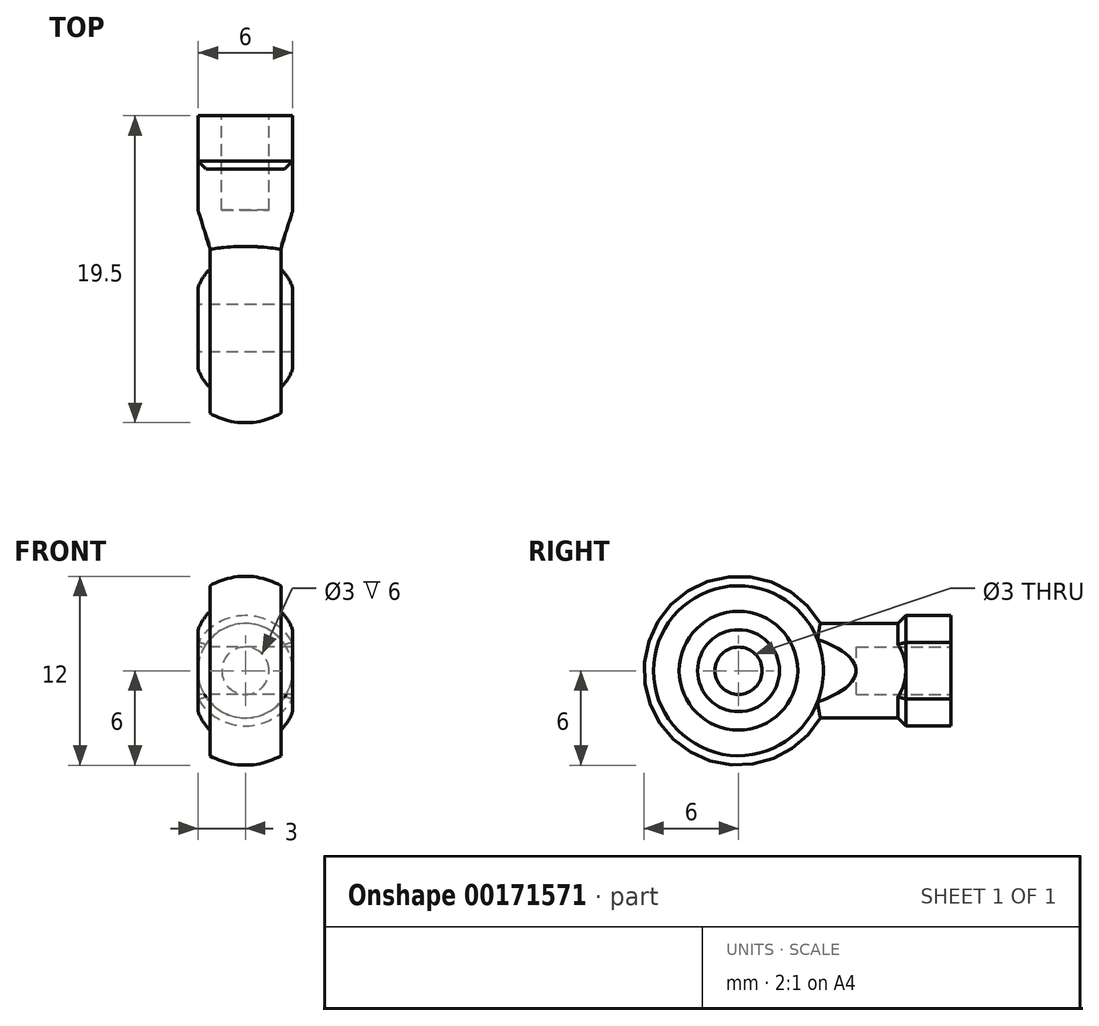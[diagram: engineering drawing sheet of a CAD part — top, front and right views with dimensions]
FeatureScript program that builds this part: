
annotation { "Feature Type Name" : "Feature", "Feature Type Description" : "" }
export const myFeature = defineFeature(function(context is Context, id is Id, definition is map)
    precondition{}
    {
        {
            assignVariable(context, id + "F0", {"name" : "L1", "anyValue" : 13.5});
        }
        {
            assignVariable(context, id + "F1", {"name" : "L2", "anyValue" : 6});
        }
        {
            assignVariable(context, id + "F2", {"name" : "AF", "anyValue" : 6});
        }
        {
            assignVariable(context, id + "F3", {"name" : "Wrench_Diam", "anyValue" : getVariable(context, 'AF') + 1});
        }
        {
            assignVariable(context, id + "F4", {"name" : "Chamfer_Size", "anyValue" : (getVariable(context, 'Wrench_Diam') - getVariable(context, 'AF')) / 2});
        }
        {
            var Q0;
            Q0=qCreatedBy(makeId("Top.planeOp"),FACE);
            var sketch = newSketch(context, id + "F5", { "sketchPlane" : qUnion([Q0])});
            skLineSegment(sketch, "E0", {"start": v(-3, 0) * mm, "end": v(3, 0) * mm, "construction": true});
            skLineSegment(sketch, "E1", {"start": v(-3, 1.5) * mm, "end": v(-3, 2.6) * mm});
            skArc(sketch, "E2", {"start": v(3, 2.6) * mm, "mid": v(0, 4.7) * mm, "end": v(-3, 2.6) * mm});
            skLineSegment(sketch, "E3", {"start": v(-3, 1.5) * mm, "end": v(3, 1.5) * mm});
            skLineSegment(sketch, "E4", {"start": v(3, 1.5) * mm, "end": v(3, 2.6) * mm});
            skLineSegment(sketch, "E5", {"start": v(-2.25, 3.77) * mm, "end": v(-2.25, 5.4) * mm});
            skArc(sketch, "E6", {"start": v(2.25, 5.4) * mm, "mid": v(0, 6) * mm, "end": v(-2.25, 5.4) * mm});
            skLineSegment(sketch, "E7", {"start": v(2.25, 5.4) * mm, "end": v(2.25, 3.77) * mm});
            skPoint(sketch, "E8.endSnap0", {"position": v(0, 4.7) * mm});
            skLineSegment(sketch, "E9", {"start": v(0, 0) * mm, "end": v(0, 6) * mm, "construction": true});
            skLineSegment(sketch, "E10", {"start": v(2.25, 5.4) * mm, "end": v(3.29, 8.25) * mm});
            skLineSegment(sketch, "E11", {"start": v(3.29, 8.25) * mm, "end": v(5, 8.25) * mm});
            skLineSegment(sketch, "E12", {"start": v(5, 8.25) * mm, "end": v(5, 1.5) * mm});
            skLineSegment(sketch, "E13", {"start": v(5, 1.5) * mm, "end": v(3, 1.5) * mm});
            skLineSegment(sketch, "E14.MirrorCS", {"start": v(-2.25, 5.4) * mm, "end": v(-3.29, 8.25) * mm});
            skLineSegment(sketch, "E15.MirrorCS", {"start": v(-3.29, 8.25) * mm, "end": v(-5, 8.25) * mm});
            skLineSegment(sketch, "E16.MirrorCS", {"start": v(-5, 8.25) * mm, "end": v(-5, 1.5) * mm});
            skLineSegment(sketch, "E17.MirrorCS", {"start": v(-5, 1.5) * mm, "end": v(-3, 1.5) * mm});
            skSolve(sketch);
        }
        {
            var Q0;
            {var subQ1=sQuery(id+"F5.wireOp",EDGE,"E1");Q0=makeQuery(id+"F5.imprint","IMPRINT",FACE,{"disambiguationData":[TD([[makeQuery(id+"F5.imprint","IMPRINT",EDGE,{"derivedFrom":subQ1}),-1.0]])]});}
            var Q1;
            {var subQ0=sQuery(id+"F5.wireOp",EDGE,"E5");Q1=makeQuery(id+"F5.imprint","IMPRINT",FACE,{"disambiguationData":[TD([[makeQuery(id+"F5.imprint","IMPRINT",EDGE,{"derivedFrom":subQ0}),-1.0]])]});}
            var Q2;
            Q2=sQuery(id+"F5.wireOp",EDGE,"E0");
            revolve(context, id + "F6", {"entities" : qUnion([Q0, Q1]), "axis" : qUnion([Q2]), "revolveType" : RevolveType.FULL});
        }
        {
            var Q0;
            Q0=qCreatedBy(makeId("Front.planeOp"),FACE);
            cPlane(context, id + "F7", {"entities" : qUnion([Q0]), "cplaneType" : CPlaneType.OFFSET, "offset" : (getVariable(context, 'L1')) * mm, "oppositeDirection" : true, "width" : 150 * mm, "height" : 150 * mm});
        }
        {
            var Q0;
            Q0=qCreatedBy(id+"F7.planeOp",FACE);
            var sketch = newSketch(context, id + "F8", { "sketchPlane" : qUnion([Q0])});
            skCircle(sketch, "E18", {"center": v(0, 0) * mm, "radius": 3 * mm});
            skArc(sketch, "E19", {"start": v(3, 1.8) * mm, "mid": v(0, 3.5) * mm, "end": v(-3, 1.8) * mm});
            skCircle(sketch, "E20", {"center": v(0, 0) * mm, "radius": 1.5 * mm});
            skLineSegment(sketch, "E21", {"start": v(3, -1.8) * mm, "end": v(3, 1.8) * mm});
            skLineSegment(sketch, "E22", {"start": v(-3, -1.8) * mm, "end": v(-3, 1.8) * mm});
            skArc(sketch, "E23.trimOffspring", {"start": v(-3, -1.8) * mm, "mid": v(0, -3.5) * mm, "end": v(3, -1.8) * mm});
            skArc(sketch, "E24", {"start": v(-3, 1.8) * mm, "mid": v(-3.5, 0) * mm, "end": v(-3, -1.8) * mm, "construction": true});
            skSolve(sketch);
        }
        {
            var Q0;
            Q0=makeQuery(id+"F8.imprint","IMPRINT",FACE,{"disambiguationData":[TD([[makeQuery(id+"F8.imprint","IMPRINT",EDGE,{"derivedFrom":sQuery(id+"F8.wireOp",EDGE,"E20")}),-1.0]])]});
            var Q1;
            Q1=makeQuery(id+"F8.imprint","IMPRINT",FACE,{"disambiguationData":[TD([[makeQuery(id+"F8.imprint","IMPRINT",EDGE,{"derivedFrom":sQuery(id+"F8.wireOp",EDGE,"E20")}),1.0]])]});
            extrude(context, id + "F9", {"entities" : qUnion([Q0, Q1]), "operationType" : NewBodyOperationType.ADD, "endBound" : BoundingType.UP_TO_NEXT, "depth" : 25 * mm});
        }
        {
            var Q0;
            {var subQ5=sQuery(id+"F8.wireOp",EDGE,"E19");Q0=makeQuery(id+"F8.imprint","IMPRINT",FACE,{"disambiguationData":[TD([[makeQuery(id+"F8.imprint","IMPRINT",EDGE,{"derivedFrom":subQ5}),1.0]])]});}
            var Q1;
            {var subQ5=sQuery(id+"F8.wireOp",EDGE,"E23.trimOffspring");Q1=makeQuery(id+"F8.imprint","IMPRINT",FACE,{"disambiguationData":[TD([[makeQuery(id+"F8.imprint","IMPRINT",EDGE,{"derivedFrom":subQ5}),1.0]])]});}
            extrude(context, id + "F10", {"entities" : qUnion([Q0, Q1]), "operationType" : NewBodyOperationType.ADD, "depth" : (getVariable(context, 'L1') / 4) * mm});
        }
        {
            var Q0;
            Q0=makeQuery(id+"F8.imprint","IMPRINT",FACE,{"disambiguationData":[TD([[makeQuery(id+"F8.imprint","IMPRINT",EDGE,{"derivedFrom":sQuery(id+"F8.wireOp",EDGE,"E20")}),1.0]])]});
            extrude(context, id + "F11", {"entities" : qUnion([Q0]), "operationType" : NewBodyOperationType.REMOVE, "depth" : (getVariable(context, 'L2')) * mm});
        }
        {
            var Q0;
            Q0=makeQuery(id+"F10.opExtrude","CAP_EDGE",EDGE,{"disambiguationData":[OSD([sQuery(id+"F8.wireOp",EDGE,"E19")])],"isStart":false});
            var Q1;
            {var subQ0=sQuery(id+"F8.wireOp",EDGE,"E21");Q1=makeQuery(id+"F10.opExtrude","CAP_EDGE",EDGE,{"disambiguationData":[OSD([subQ0]),TDD([makeQuery(id+"F8.imprint","IMPRINT",EDGE,{"disambiguationData":[TD([[makeQuery(id+"F8.imprint","INTERSECT",VERTEX,{"derivedFrom":[sQuery(id+"F8.wireOp",EDGE,"E19"),subQ0]}),1.0]])],"derivedFrom":subQ0})])],"isStart":false});}
            var Q2;
            {var subQ0=sQuery(id+"F8.wireOp",EDGE,"E22");Q2=makeQuery(id+"F10.opExtrude","CAP_EDGE",EDGE,{"disambiguationData":[OSD([subQ0]),TDD([makeQuery(id+"F8.imprint","IMPRINT",EDGE,{"disambiguationData":[TD([[makeQuery(id+"F8.imprint","INTERSECT",VERTEX,{"derivedFrom":[sQuery(id+"F8.wireOp",EDGE,"E19"),subQ0]}),1.0]])],"derivedFrom":subQ0})])],"isStart":false});}
            var Q3;
            Q3=makeQuery(id+"F10.opExtrude","CAP_EDGE",EDGE,{"disambiguationData":[OSD([sQuery(id+"F8.wireOp",EDGE,"E23.trimOffspring")])],"isStart":false});
            var Q4;
            {var subQ0=sQuery(id+"F8.wireOp",EDGE,"E21");Q4=makeQuery(id+"F10.opExtrude","CAP_EDGE",EDGE,{"disambiguationData":[OSD([subQ0]),TDD([makeQuery(id+"F8.imprint","IMPRINT",EDGE,{"disambiguationData":[TD([[makeQuery(id+"F8.imprint","INTERSECT",VERTEX,{"derivedFrom":[subQ0,sQuery(id+"F8.wireOp",EDGE,"E23.trimOffspring")]}),-1.0]])],"derivedFrom":subQ0})])],"isStart":false});}
            var Q5;
            {var subQ0=sQuery(id+"F8.wireOp",EDGE,"E22");Q5=makeQuery(id+"F10.opExtrude","CAP_EDGE",EDGE,{"disambiguationData":[OSD([subQ0]),TDD([makeQuery(id+"F8.imprint","IMPRINT",EDGE,{"disambiguationData":[TD([[makeQuery(id+"F8.imprint","INTERSECT",VERTEX,{"derivedFrom":[subQ0,sQuery(id+"F8.wireOp",EDGE,"E23.trimOffspring")]}),-1.0]])],"derivedFrom":subQ0})])],"isStart":false});}
            chamfer(context, id + "F12", {"entities" : qUnion([Q0, Q1, Q2, Q3, Q4, Q5]), "width" : (getVariable(context, 'Chamfer_Size')) * mm, "tangentPropagation" : true});
        }
        {
            var Q0;
            {var subQ1=sQuery(id+"F5.wireOp",EDGE,"E4");Q0=makeQuery(id+"F5.imprint","IMPRINT",FACE,{"disambiguationData":[TD([[makeQuery(id+"F5.imprint","IMPRINT",EDGE,{"derivedFrom":subQ1}),-1.0]])]});}
            var Q1;
            {var subQ2=sQuery(id+"F5.wireOp",EDGE,"E1");Q1=makeQuery(id+"F5.imprint","IMPRINT",FACE,{"disambiguationData":[TD([[makeQuery(id+"F5.imprint","IMPRINT",EDGE,{"derivedFrom":subQ2}),1.0]])]});}
            var Q2;
            Q2=sQuery(id+"F5.wireOp",EDGE,"E0");
            revolve(context, id + "F13", {"operationType" : NewBodyOperationType.REMOVE, "entities" : qUnion([Q0, Q1]), "axis" : qUnion([Q2]), "revolveType" : RevolveType.FULL, "oppositeDirection" : true});
        }
    });
